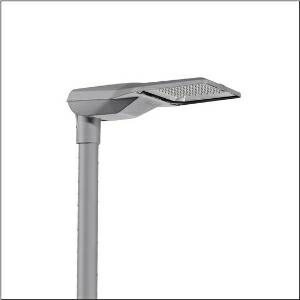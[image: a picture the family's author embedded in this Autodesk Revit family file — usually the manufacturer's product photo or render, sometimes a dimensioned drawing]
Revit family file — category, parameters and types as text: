
# Revit family: streetlight_sl_21_iq_midi___stw1_0a_5xe3e31g08nb_66c1
name_source: partatom
category: Lighting Fixtures
units: mm (PartAtom-declared; Revit-internal decimal feet)

## family parameters
Cut with Voids When Loaded = No
Host = Face
Light Source = No
Part Type = Normal
Room Calculation Point = No
Round Connector Dimension = Use Diameter
Shared = No

## types (1)
- --- (1 x LED, 23230 lm, 155.5 W, 3000K)
    Apparent Load = 155 VA
    CIE Flux Codes = 39 75 98 100 100
    Color Rendering = 70
    Color Temperature = 3000K
    Default Elevation = 1800 mm
    Description = Streetlight SL 21 iQ midi, mast luminaire, primary light control with lens, of PMMA, primary optical cover: cover, of toughened safety glass, transparent, light distribution: STW1.0a, light emission: direct distribution, primary light characteristic: asymmetric, installation type: post-top, side-entry, LED, High Power LED, rated luminous flux: 23.230lm, luminous efficacy: 149lm/W, light colour: 730, colour temperature: 3000K, control gear: iQ Street-Remote, control: Street-Remote, Auto-Match, Temp-Guard, Lumen-Switch, Night-Set, Smart-Wire, Light-Fading, Desk-Remote (wireless, voltage-free reading and setting of iQ features in the workshop via application-optimized NFC function/RFID function), optimised constant luminous flux control (CLO 2.0), pre-setting: linear dimming characteristic, mains connection: 230..240V, AC, 50/60Hz, start of lifetime: 156W, end of service life: 162W, reduction: 69W, luminaire housing, of diecast aluminium, powder-coated, SITECO metallic grey (DB 702S), corrosivity category C5 high according to DIN EN ISO 12944, please order mast flange separately, inclination adjustable: 0°, 5°, 10°, 15°, sealing non-destructively replaceable, multi-level sealing system, length: 644mm, width: 335mm, height: 110mm, mast flange for spigot size: 42mm (side-entry): 5XC10008XM4, 60/48mm (side-entry/post-top): 5XC10108XM2, 76/60mm (side-entry/post-top): 5XC10108XM1, mounting height: 4..8m, protection rating (complete): IP66, insulation class (complete): insulation class II (safety insulation), certification: CE, ENEC, ENEC+, VDE, impact resistance: IK10, permissible operating ambient temperature for outdoor applications: -40..+50°C, standard-compliant lighting for roads and squares, packaging unit: 1 piece

Light Distribution: STW1.0a
    Height = 111 mm
    Lamp = 1 x LED
    Lamp Light Flux = 23230 lm
    Lamp Power = 155.5 W
    Lamp count = 1
    Length = 644 mm
    Luminous efficacy = 149 lm/W
    Manufacturer = Siteco
    ModVariant = No
    Model = 5XE3E31G08NB
    Number of Poles = 1
    OnlyDefault = Yes
    Power Factor = 1
    Product Name = Streetlight SL 21 iQ midi | STW1.0a
    Product group = mast luminaire | pylon top
    ProductGroupID = 6100
    Protection Class = Protection class II
    Protection Degree = IP 66
    RLX_Detail_Level = 1
    RLX_Emergency_Light_Flux = 0 lm
    RLX_Emergency_Type = 0
    RLX_Emergency_Type_DB = No
    RlxData = <blob elided: 27289 chars, md5=8dd186c9>
    Socket = socket
    Standby Power = 0 W
    System Light Flux = 23230 lm
    System Power = 155 W
    Type Comments = factory setting: luminous flux: 100 % | dim-lin: 254 | 823 mA
    Type Image = l_1004298.jpg
    URL = http://relux.com
    VarID = @adj_169361
    Voltage = 0 V
    Weight = 0.00 kg
    Width = 336 mm

## geometry (parser evidence)
native form markers: Blend x4, Sweep x11
no freeform markers — native parametric forms only
